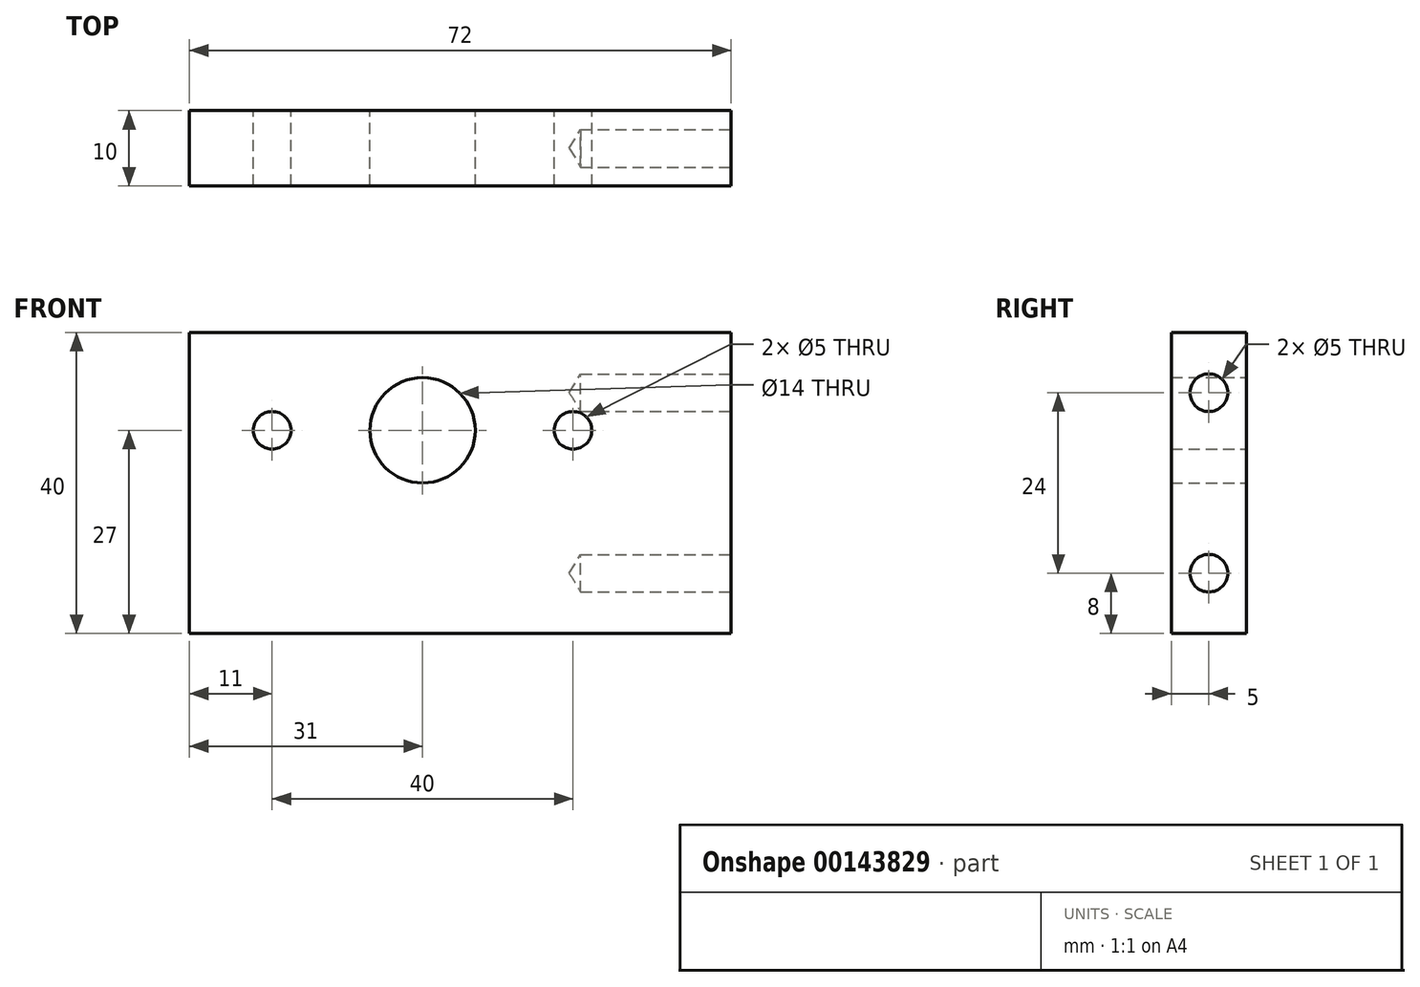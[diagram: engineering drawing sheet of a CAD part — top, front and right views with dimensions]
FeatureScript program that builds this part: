
annotation { "Feature Type Name" : "Feature", "Feature Type Description" : "" }
export const myFeature = defineFeature(function(context is Context, id is Id, definition is map)
    precondition{}
    {
        {
            var Q0;
            Q0=qCreatedBy(makeId("Front.planeOp"),FACE);
            var sketch = newSketch(context, id + "F0", { "sketchPlane" : qUnion([Q0])});
            skLineSegment(sketch, "E0.bottom", {"start": v(36, -20) * mm, "end": v(-36, -20) * mm});
            skLineSegment(sketch, "E0.top", {"start": v(36, 20) * mm, "end": v(-36, 20) * mm});
            skLineSegment(sketch, "E0.left", {"start": v(36, -20) * mm, "end": v(36, 20) * mm});
            skLineSegment(sketch, "E0.right", {"start": v(-36, -20) * mm, "end": v(-36, 20) * mm});
            skPoint(sketch, "E0.middle", {"position": v(0, 0) * mm});
            skCircle(sketch, "E1", {"center": v(-5, 7) * mm, "radius": 7 * mm});
            skCircle(sketch, "E2", {"center": v(-25, 7) * mm, "radius": 2.5 * mm});
            skCircle(sketch, "E3", {"center": v(15, 7) * mm, "radius": 2.5 * mm});
            skSolve(sketch);
        }
        {
            var Q0;
            Q0=makeQuery(id+"F0.imprint","IMPRINT",FACE,{"disambiguationData":[TD([[makeQuery(id+"F0.imprint","IMPRINT",EDGE,{"derivedFrom":sQuery(id+"F0.wireOp",EDGE,"E0.bottom")}),-1.0]])]});
            extrude(context, id + "F1", {"entities" : qUnion([Q0]), "depth" : 10 * mm});
        }
        {
            var Q0;
            Q0=makeQuery(id+"F1.opExtrude","SWEPT_FACE",FACE,{"disambiguationData":[OSD([sQuery(id+"F0.wireOp",EDGE,"E0.left")])]});
            var sketch = newSketch(context, id + "F2", { "sketchPlane" : qUnion([Q0])});
            skCircle(sketch, "E4", {"center": v(-5, 12) * mm, "radius": 2.59 * mm});
            skCircle(sketch, "E5", {"center": v(-5, -12) * mm, "radius": 2.86 * mm});
            skSolve(sketch);
        }
        {
            var Q0;
            Q0=sQuery(id+"F2.wireOp",VERTEX,"E4.center");
            var Q1;
            Q1=sQuery(id+"F2.wireOp",VERTEX,"E5.center");
            var Q2;
            Q2=makeQuery(id+"F1.opExtrude","SWEPT_BODY",BODY,{"disambiguationData":[OSD([sQuery(id+"F0.wireOp",EDGE,"E0.bottom"),sQuery(id+"F0.wireOp",EDGE,"E0.top"),sQuery(id+"F0.wireOp",EDGE,"E0.left"),sQuery(id+"F0.wireOp",EDGE,"E0.right"),sQuery(id+"F0.wireOp",EDGE,"E1"),sQuery(id+"F0.wireOp",EDGE,"E2"),sQuery(id+"F0.wireOp",EDGE,"E3")])]});
            hole(context, id + "F3", {"style" : HoleStyle.SIMPLE, "endStyle" : HoleEndStyle.BLIND, "standardTappedOrClearance" : lookupTablePath({ "standard" : "ISO", "engagement" : "75%", "pitch" : "1 mm", "size" : "M6", "type" : "Tapped" }), "standardBlindInLast" : lookupTablePath({ "standard" : "ISO", "engagement" : "75%", "pitch" : "1 mm", "size" : "M6", "type" : "Tapped" }), "holeDiameter" : 5 * mm, "holeDepth" : 20 * mm, "startFromSketch" : true, "locations" : qUnion([Q0, Q1]), "scope" : qUnion([Q2]), "majorDiameter" : 6 * mm});
        }
    });
